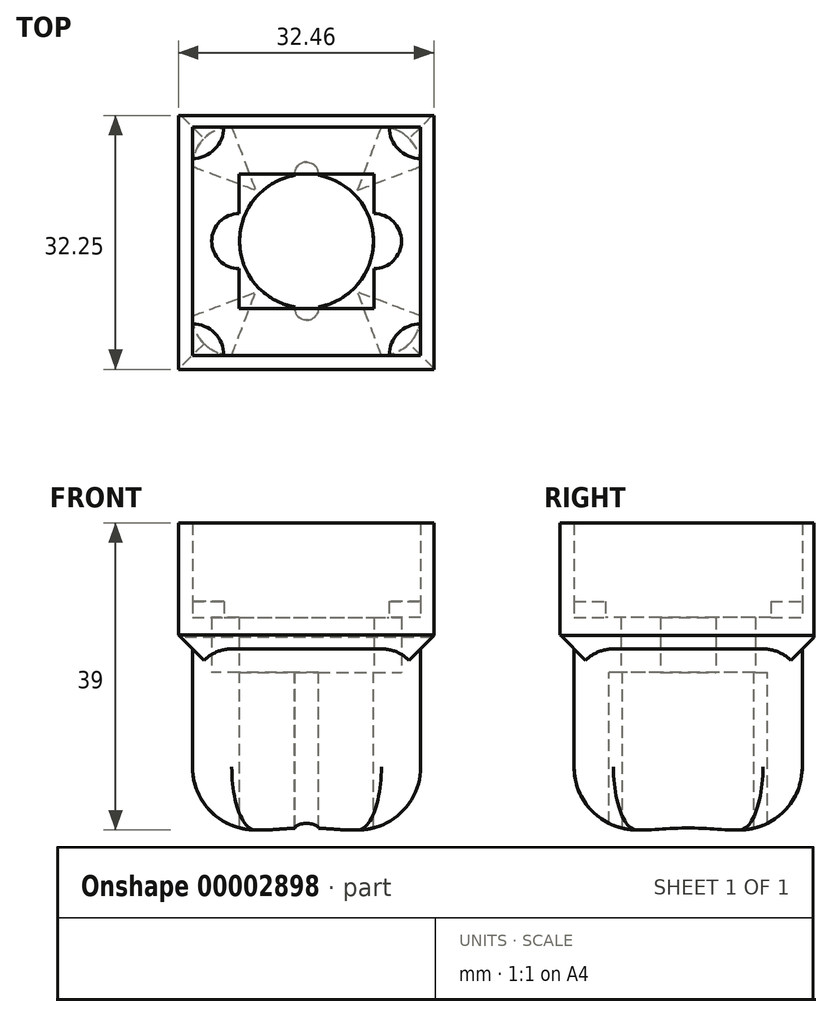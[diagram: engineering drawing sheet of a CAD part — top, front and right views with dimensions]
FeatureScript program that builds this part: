
annotation { "Feature Type Name" : "Feature", "Feature Type Description" : "" }
export const myFeature = defineFeature(function(context is Context, id is Id, definition is map)
    precondition{}
    {
        {
            var Q0;
            Q0=qCreatedBy(makeId("Top.planeOp"),FACE);
            var sketch = newSketch(context, id + "F0", { "sketchPlane" : qUnion([Q0])});
            skLineSegment(sketch, "E0.bottom", {"start": v(-49.13, 7.76) * mm, "end": v(-32.03, 7.76) * mm});
            skLineSegment(sketch, "E0.top", {"start": v(-49.13, -9.34) * mm, "end": v(-32.03, -9.34) * mm});
            skLineSegment(sketch, "E0.left", {"start": v(-49.13, 7.76) * mm, "end": v(-49.13, 2.7) * mm});
            skLineSegment(sketch, "E0.right", {"start": v(-32.03, 7.76) * mm, "end": v(-32.03, 2.7) * mm});
            skLineSegment(sketch, "E1.bottom", {"start": v(-55.08, 13.7) * mm, "end": v(-26.08, 13.7) * mm});
            skLineSegment(sketch, "E1.top", {"start": v(-55.08, -15.3) * mm, "end": v(-26.08, -15.3) * mm});
            skLineSegment(sketch, "E1.left", {"start": v(-55.08, 13.7) * mm, "end": v(-55.08, -15.3) * mm});
            skLineSegment(sketch, "E1.right", {"start": v(-26.08, 13.7) * mm, "end": v(-26.08, -15.3) * mm});
            skArc(sketch, "E2", {"start": v(-32.03, -4.3) * mm, "mid": v(-28.53, -0.8) * mm, "end": v(-32.03, 2.7) * mm});
            skArc(sketch, "E3", {"start": v(-49.13, 2.7) * mm, "mid": v(-52.63, -0.8) * mm, "end": v(-49.13, -4.3) * mm});
            skLineSegment(sketch, "E4.trimOffspring", {"start": v(-49.13, -4.3) * mm, "end": v(-49.13, -9.34) * mm});
            skLineSegment(sketch, "E5.trimOffspring", {"start": v(-32.03, -4.3) * mm, "end": v(-32.03, -9.34) * mm});
            skSolve(sketch);
        }
        {
            var Q0;
            Q0 = qSketchRegion(id + "F0", true);
            extrude(context, id + "F1", {"entities" : qUnion([Q0]), "depth" : 7 * mm});
        }
        {
            var Q0;
            Q0=qCreatedBy(makeId("Top.planeOp"),FACE);
            var sketch = newSketch(context, id + "F2", { "sketchPlane" : qUnion([Q0])});
            skLineSegment(sketch, "E6", {"start": v(-55.08, 13.7) * mm, "end": v(-26.08, 13.7) * mm});
            skLineSegment(sketch, "E7", {"start": v(-26.08, 13.7) * mm, "end": v(-26.08, -15.3) * mm});
            skLineSegment(sketch, "E8", {"start": v(-26.08, -15.3) * mm, "end": v(-55.08, -15.3) * mm});
            skLineSegment(sketch, "E9", {"start": v(-55.08, -15.3) * mm, "end": v(-55.08, 13.7) * mm});
            skArc(sketch, "E10", {"start": v(-42.07, 7.57) * mm, "mid": v(-49.08, -0.8) * mm, "end": v(-42.07, -9.16) * mm});
            skArc(sketch, "E11", {"start": v(-39.1, 7.57) * mm, "mid": v(-40.58, 9.26) * mm, "end": v(-42.07, 7.57) * mm});
            skArc(sketch, "E12", {"start": v(-42.07, -9.16) * mm, "mid": v(-40.58, -10.84) * mm, "end": v(-39.1, -9.16) * mm});
            skArc(sketch, "E13.trimOffspring", {"start": v(-39.1, -9.16) * mm, "mid": v(-32.08, -0.8) * mm, "end": v(-39.1, 7.57) * mm});
            skSolve(sketch);
        }
        {
            var Q0;
            Q0 = qSketchRegion(id + "F2", true);
            extrude(context, id + "F3", {"entities" : qUnion([Q0]), "operationType" : NewBodyOperationType.ADD, "oppositeDirection" : true, "depth" : 20 * mm});
        }
        {
            var Q0;
            Q0=makeQuery(id+"F3.opExtrude","CAP_EDGE",EDGE,{"disambiguationData":[OSD([sQuery(id+"F2.wireOp",EDGE,"E6")])],"isStart":false});
            var Q1;
            Q1=makeQuery(id+"F3.opExtrude","CAP_EDGE",EDGE,{"disambiguationData":[OSD([sQuery(id+"F2.wireOp",EDGE,"E7")])],"isStart":false});
            var Q2;
            Q2=makeQuery(id+"F3.opExtrude","CAP_EDGE",EDGE,{"disambiguationData":[OSD([sQuery(id+"F2.wireOp",EDGE,"E8")])],"isStart":false});
            var Q3;
            Q3=makeQuery(id+"F3.opExtrude","CAP_EDGE",EDGE,{"disambiguationData":[OSD([sQuery(id+"F2.wireOp",EDGE,"E9")])],"isStart":false});
            fillet(context, id + "F4", {"entities" : qUnion([Q0, Q1, Q2, Q3]), "radius" : 8 * mm, "tangentPropagation" : true, "allowEdgeOverflow" : false});
        }
        {
            var Q0;
            Q0=makeQuery(id+"F1.opExtrude","CAP_FACE",FACE,{"disambiguationData":[OSD([sQuery(id+"F0.wireOp",EDGE,"E0.bottom"),sQuery(id+"F0.wireOp",EDGE,"E0.top"),sQuery(id+"F0.wireOp",EDGE,"E0.left"),sQuery(id+"F0.wireOp",EDGE,"E0.right"),sQuery(id+"F0.wireOp",EDGE,"E1.bottom"),sQuery(id+"F0.wireOp",EDGE,"E1.top"),sQuery(id+"F0.wireOp",EDGE,"E1.left"),sQuery(id+"F0.wireOp",EDGE,"E1.right"),sQuery(id+"F0.wireOp",EDGE,"E2"),sQuery(id+"F0.wireOp",EDGE,"E3"),sQuery(id+"F0.wireOp",EDGE,"E4.trimOffspring"),sQuery(id+"F0.wireOp",EDGE,"E5.trimOffspring")])],"isStart":false});
            var sketch = newSketch(context, id + "F5", { "sketchPlane" : qUnion([Q0])});
            skArc(sketch, "E14", {"start": v(-55.08, 9.7) * mm, "mid": v(-52.25, 10.88) * mm, "end": v(-51.08, 13.7) * mm});
            skArc(sketch, "E15", {"start": v(-30.08, 13.7) * mm, "mid": v(-28.9, 10.88) * mm, "end": v(-26.08, 9.7) * mm});
            skArc(sketch, "E16", {"start": v(-26.08, -11.3) * mm, "mid": v(-28.9, -12.47) * mm, "end": v(-30.08, -15.3) * mm});
            skArc(sketch, "E17", {"start": v(-51.08, -15.3) * mm, "mid": v(-52.25, -12.47) * mm, "end": v(-55.08, -11.3) * mm});
            skLineSegment(sketch, "E18.bottom", {"start": v(-56.86, 15.16) * mm, "end": v(-24.4, 15.16) * mm});
            skLineSegment(sketch, "E18.top", {"start": v(-56.86, -17.1) * mm, "end": v(-24.4, -17.1) * mm});
            skLineSegment(sketch, "E18.left", {"start": v(-56.86, 15.16) * mm, "end": v(-56.86, -17.1) * mm});
            skLineSegment(sketch, "E18.right", {"start": v(-24.4, 15.16) * mm, "end": v(-24.4, -17.1) * mm});
            skLineSegment(sketch, "E19", {"start": v(-51.08, 13.7) * mm, "end": v(-30.08, 13.7) * mm});
            skLineSegment(sketch, "E20", {"start": v(-26.08, 9.7) * mm, "end": v(-26.08, -11.3) * mm});
            skLineSegment(sketch, "E21", {"start": v(-30.08, -15.3) * mm, "end": v(-51.08, -15.3) * mm});
            skLineSegment(sketch, "E22", {"start": v(-55.08, -11.3) * mm, "end": v(-55.08, 9.7) * mm});
            skSolve(sketch);
        }
        {
            var Q0;
            Q0=makeQuery(id+"F5.imprint","IMPRINT",FACE,{"disambiguationData":[TD([[makeQuery(id+"F5.imprint","IMPRINT",EDGE,{"derivedFrom":sQuery(id+"F5.wireOp",EDGE,"E18.bottom")}),-1.0]])]});
            var Q1;
            {var subQ1=sQuery(id+"F5.wireOp",EDGE,"E15");Q1=makeQuery(id+"F5.imprint","IMPRINT",FACE,{"disambiguationData":[TD([[makeQuery(id+"F5.imprint","IMPRINT",EDGE,{"derivedFrom":subQ1}),1.0]])]});}
            var Q2;
            {var subQ1=sQuery(id+"F5.wireOp",EDGE,"E14");Q2=makeQuery(id+"F5.imprint","IMPRINT",FACE,{"disambiguationData":[TD([[makeQuery(id+"F5.imprint","IMPRINT",EDGE,{"derivedFrom":subQ1}),1.0]])]});}
            var Q3;
            {var subQ1=sQuery(id+"F5.wireOp",EDGE,"E17");Q3=makeQuery(id+"F5.imprint","IMPRINT",FACE,{"disambiguationData":[TD([[makeQuery(id+"F5.imprint","IMPRINT",EDGE,{"derivedFrom":subQ1}),1.0]])]});}
            var Q4;
            {var subQ1=sQuery(id+"F5.wireOp",EDGE,"E16");Q4=makeQuery(id+"F5.imprint","IMPRINT",FACE,{"disambiguationData":[TD([[makeQuery(id+"F5.imprint","IMPRINT",EDGE,{"derivedFrom":subQ1}),1.0]])]});}
            extrude(context, id + "F6", {"entities" : qUnion([Q0, Q1, Q2, Q3, Q4]), "operationType" : NewBodyOperationType.ADD, "endBound" : BoundingType.SYMMETRIC, "depth" : 4 * mm});
        }
        {
            var Q0;
            Q0=makeQuery(id+"F6.boolean.opBoolean","INTERSECT",EDGE,{"derivedFrom":[makeQuery(id+"F3.boolean.opBoolean","MERGE",FACE,{"derivedFrom":[makeQuery(id+"F1.opExtrude","SWEPT_FACE",FACE,{"disambiguationData":[OSD([sQuery(id+"F0.wireOp",EDGE,"E1.top")])]}),makeQuery(id+"F3.opExtrude","SWEPT_FACE",FACE,{"disambiguationData":[OSD([sQuery(id+"F2.wireOp",EDGE,"E8")])]})]}),makeQuery(id+"F6.opExtrude","CAP_FACE",FACE,{"disambiguationData":[OSD([sQuery(id+"F5.wireOp",EDGE,"E14"),sQuery(id+"F5.wireOp",EDGE,"E15"),sQuery(id+"F5.wireOp",EDGE,"E16"),sQuery(id+"F5.wireOp",EDGE,"E17"),sQuery(id+"F5.wireOp",EDGE,"E18.bottom"),sQuery(id+"F5.wireOp",EDGE,"E18.top"),sQuery(id+"F5.wireOp",EDGE,"E18.left"),sQuery(id+"F5.wireOp",EDGE,"E18.right"),sQuery(id+"F5.wireOp",EDGE,"E19"),sQuery(id+"F5.wireOp",EDGE,"E20"),sQuery(id+"F5.wireOp",EDGE,"E21"),sQuery(id+"F5.wireOp",EDGE,"E22")])],"isStart":true})]});
            var Q1;
            Q1=makeQuery(id+"F6.boolean.opBoolean","INTERSECT",EDGE,{"derivedFrom":[makeQuery(id+"F3.boolean.opBoolean","MERGE",FACE,{"derivedFrom":[makeQuery(id+"F1.opExtrude","SWEPT_FACE",FACE,{"disambiguationData":[OSD([sQuery(id+"F0.wireOp",EDGE,"E1.right")])]}),makeQuery(id+"F3.opExtrude","SWEPT_FACE",FACE,{"disambiguationData":[OSD([sQuery(id+"F2.wireOp",EDGE,"E7")])]})]}),makeQuery(id+"F6.opExtrude","CAP_FACE",FACE,{"disambiguationData":[OSD([sQuery(id+"F5.wireOp",EDGE,"E14"),sQuery(id+"F5.wireOp",EDGE,"E15"),sQuery(id+"F5.wireOp",EDGE,"E16"),sQuery(id+"F5.wireOp",EDGE,"E17"),sQuery(id+"F5.wireOp",EDGE,"E18.bottom"),sQuery(id+"F5.wireOp",EDGE,"E18.top"),sQuery(id+"F5.wireOp",EDGE,"E18.left"),sQuery(id+"F5.wireOp",EDGE,"E18.right"),sQuery(id+"F5.wireOp",EDGE,"E19"),sQuery(id+"F5.wireOp",EDGE,"E20"),sQuery(id+"F5.wireOp",EDGE,"E21"),sQuery(id+"F5.wireOp",EDGE,"E22")])],"isStart":true})]});
            var Q2;
            Q2=makeQuery(id+"F6.boolean.opBoolean","INTERSECT",EDGE,{"derivedFrom":[makeQuery(id+"F3.boolean.opBoolean","MERGE",FACE,{"derivedFrom":[makeQuery(id+"F1.opExtrude","SWEPT_FACE",FACE,{"disambiguationData":[OSD([sQuery(id+"F0.wireOp",EDGE,"E1.bottom")])]}),makeQuery(id+"F3.opExtrude","SWEPT_FACE",FACE,{"disambiguationData":[OSD([sQuery(id+"F2.wireOp",EDGE,"E6")])]})]}),makeQuery(id+"F6.opExtrude","CAP_FACE",FACE,{"disambiguationData":[OSD([sQuery(id+"F5.wireOp",EDGE,"E14"),sQuery(id+"F5.wireOp",EDGE,"E15"),sQuery(id+"F5.wireOp",EDGE,"E16"),sQuery(id+"F5.wireOp",EDGE,"E17"),sQuery(id+"F5.wireOp",EDGE,"E18.bottom"),sQuery(id+"F5.wireOp",EDGE,"E18.top"),sQuery(id+"F5.wireOp",EDGE,"E18.left"),sQuery(id+"F5.wireOp",EDGE,"E18.right"),sQuery(id+"F5.wireOp",EDGE,"E19"),sQuery(id+"F5.wireOp",EDGE,"E20"),sQuery(id+"F5.wireOp",EDGE,"E21"),sQuery(id+"F5.wireOp",EDGE,"E22")])],"isStart":true})]});
            var Q3;
            Q3=makeQuery(id+"F6.boolean.opBoolean","INTERSECT",EDGE,{"derivedFrom":[makeQuery(id+"F3.boolean.opBoolean","MERGE",FACE,{"derivedFrom":[makeQuery(id+"F1.opExtrude","SWEPT_FACE",FACE,{"disambiguationData":[OSD([sQuery(id+"F0.wireOp",EDGE,"E1.left")])]}),makeQuery(id+"F3.opExtrude","SWEPT_FACE",FACE,{"disambiguationData":[OSD([sQuery(id+"F2.wireOp",EDGE,"E9")])]})]}),makeQuery(id+"F6.opExtrude","CAP_FACE",FACE,{"disambiguationData":[OSD([sQuery(id+"F5.wireOp",EDGE,"E14"),sQuery(id+"F5.wireOp",EDGE,"E15"),sQuery(id+"F5.wireOp",EDGE,"E16"),sQuery(id+"F5.wireOp",EDGE,"E17"),sQuery(id+"F5.wireOp",EDGE,"E18.bottom"),sQuery(id+"F5.wireOp",EDGE,"E18.top"),sQuery(id+"F5.wireOp",EDGE,"E18.left"),sQuery(id+"F5.wireOp",EDGE,"E18.right"),sQuery(id+"F5.wireOp",EDGE,"E19"),sQuery(id+"F5.wireOp",EDGE,"E20"),sQuery(id+"F5.wireOp",EDGE,"E21"),sQuery(id+"F5.wireOp",EDGE,"E22")])],"isStart":true})]});
            chamfer(context, id + "F7", {"entities" : qUnion([Q0, Q1, Q2, Q3]), "width" : 2 * mm, "tangentPropagation" : true});
        }
        {
            var Q0;
            Q0=makeQuery(id+"F6.opExtrude","CAP_FACE",FACE,{"disambiguationData":[OSD([sQuery(id+"F5.wireOp",EDGE,"E14"),sQuery(id+"F5.wireOp",EDGE,"E15"),sQuery(id+"F5.wireOp",EDGE,"E16"),sQuery(id+"F5.wireOp",EDGE,"E17"),sQuery(id+"F5.wireOp",EDGE,"E18.bottom"),sQuery(id+"F5.wireOp",EDGE,"E18.top"),sQuery(id+"F5.wireOp",EDGE,"E18.left"),sQuery(id+"F5.wireOp",EDGE,"E18.right"),sQuery(id+"F5.wireOp",EDGE,"E19"),sQuery(id+"F5.wireOp",EDGE,"E20"),sQuery(id+"F5.wireOp",EDGE,"E21"),sQuery(id+"F5.wireOp",EDGE,"E22")])],"isStart":false});
            var sketch = newSketch(context, id + "F8", { "sketchPlane" : qUnion([Q0])});
            skLineSegment(sketch, "E23.bottom", {"start": v(-56.86, 15.16) * mm, "end": v(-24.4, 15.16) * mm});
            skLineSegment(sketch, "E23.top", {"start": v(-56.86, -17.1) * mm, "end": v(-24.4, -17.1) * mm});
            skLineSegment(sketch, "E23.left", {"start": v(-56.86, 15.16) * mm, "end": v(-56.86, -17.1) * mm});
            skLineSegment(sketch, "E23.right", {"start": v(-24.4, 15.16) * mm, "end": v(-24.4, -17.1) * mm});
            skLineSegment(sketch, "E24.bottom", {"start": v(-26.08, -15.3) * mm, "end": v(-55.08, -15.3) * mm});
            skLineSegment(sketch, "E24.top", {"start": v(-26.08, 13.7) * mm, "end": v(-55.08, 13.7) * mm});
            skLineSegment(sketch, "E24.left", {"start": v(-26.08, -15.3) * mm, "end": v(-26.08, 13.7) * mm});
            skLineSegment(sketch, "E24.right", {"start": v(-55.08, -15.3) * mm, "end": v(-55.08, 13.7) * mm});
            skSolve(sketch);
        }
        {
            var Q0;
            Q0=makeQuery(id+"F8.imprint","IMPRINT",FACE,{"disambiguationData":[TD([[makeQuery(id+"F8.imprint","IMPRINT",EDGE,{"derivedFrom":sQuery(id+"F8.wireOp",EDGE,"E23.bottom")}),-1.0]])]});
            extrude(context, id + "F9", {"entities" : qUnion([Q0]), "operationType" : NewBodyOperationType.ADD, "depth" : 10 * mm});
        }
        {
            var Q0;
            Q0=makeQuery(id+"F3.boolean.opBoolean","MERGE",EDGE,{"derivedFrom":[makeQuery(id+"F1.opExtrude","SWEPT_EDGE",EDGE,{"disambiguationData":[OSD([sQuery(id+"F0.wireOp",EDGE,"E1.top"),sQuery(id+"F0.wireOp",EDGE,"E1.right")])]}),makeQuery(id+"F3.opExtrude","SWEPT_EDGE",EDGE,{"disambiguationData":[OSD([sQuery(id+"F2.wireOp",EDGE,"E7"),sQuery(id+"F2.wireOp",EDGE,"E8")])]})]});
            var Q1;
            Q1=makeQuery(id+"F3.boolean.opBoolean","MERGE",EDGE,{"derivedFrom":[makeQuery(id+"F1.opExtrude","SWEPT_EDGE",EDGE,{"disambiguationData":[OSD([sQuery(id+"F0.wireOp",EDGE,"E1.bottom"),sQuery(id+"F0.wireOp",EDGE,"E1.right")])]}),makeQuery(id+"F3.opExtrude","SWEPT_EDGE",EDGE,{"disambiguationData":[OSD([sQuery(id+"F2.wireOp",EDGE,"E6"),sQuery(id+"F2.wireOp",EDGE,"E7")])]})]});
            var Q2;
            Q2=makeQuery(id+"F3.boolean.opBoolean","MERGE",EDGE,{"derivedFrom":[makeQuery(id+"F1.opExtrude","SWEPT_EDGE",EDGE,{"disambiguationData":[OSD([sQuery(id+"F0.wireOp",EDGE,"E1.bottom"),sQuery(id+"F0.wireOp",EDGE,"E1.left")])]}),makeQuery(id+"F3.opExtrude","SWEPT_EDGE",EDGE,{"disambiguationData":[OSD([sQuery(id+"F2.wireOp",EDGE,"E6"),sQuery(id+"F2.wireOp",EDGE,"E9")])]})]});
            var Q3;
            Q3=makeQuery(id+"F3.boolean.opBoolean","MERGE",EDGE,{"derivedFrom":[makeQuery(id+"F1.opExtrude","SWEPT_EDGE",EDGE,{"disambiguationData":[OSD([sQuery(id+"F0.wireOp",EDGE,"E1.top"),sQuery(id+"F0.wireOp",EDGE,"E1.left")])]}),makeQuery(id+"F3.opExtrude","SWEPT_EDGE",EDGE,{"disambiguationData":[OSD([sQuery(id+"F2.wireOp",EDGE,"E8"),sQuery(id+"F2.wireOp",EDGE,"E9")])]})]});
            fillet(context, id + "F10", {"entities" : qUnion([Q0, Q1, Q2, Q3]), "radius" : 5 * mm, "tangentPropagation" : true, "allowEdgeOverflow" : false});
        }
    });
